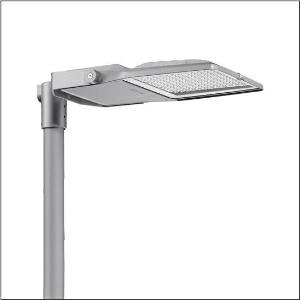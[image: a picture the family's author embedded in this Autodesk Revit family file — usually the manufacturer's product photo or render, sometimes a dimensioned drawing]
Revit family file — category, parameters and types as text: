
# Revit family: floodlight_fl_21_iq_midi___pl64_5xa7781f4e3a_1626
name_source: partatom
category: Lighting Fixtures
units: mm (PartAtom-declared; Revit-internal decimal feet)

## family parameters
Cut with Voids When Loaded = No
Host = Face
Light Source = No
Part Type = Normal
Room Calculation Point = No
Round Connector Dimension = Use Diameter
Shared = No

## types (1)
- --- (1 x LED, 36050 lm, 270.2 W, 4000K)
    Apparent Load = 270 VA
    CIE Flux Codes = 28 80 98 100 100
    Color Rendering = 70
    Color Temperature = 4000K
    Default Elevation = 1800 mm
    Description = Floodlight FL 21 iQ midi, floodlight, primary light control with lens, of PMMA, primary optical cover: protective disc, of toughened safety glass, transparent, light distribution: PL64, light emission: direct distribution, installation type: surface-mounted, lamps: LED, High Power LED, rated values: 36.050lm | 270,2W | 133,4lm/W (begin service life); end service life: 36.050lm | 286,6W; at 50% lumin. flux: 18.025lm | 117,7W | 153,1lm/W, colour temperature: 4000K, colour rendering: CRI > 70, light colour: 740, light setting 1 begin service life: 100% | 36.050lm | 270,2W | 133,4lm/W | 4.000K, light setting 1 end service life: 286,6W, further light settings possible, control: optimised constant luminous flux control (CLO 2.0), Desk-Remote (wireless, voltage-free reading and setting of iQ features in the workshop via application-optimized NFC function/RFID function), Light-Fading, Smart-Wire, Night-Set, Lumen-Switch, Temp-Guard, Auto-Match, with terminal, 6-pole, mains connection: 220..240V, AC, 50/60Hz, luminaire housing, of diecast aluminium, powder-coated, Siteco® metallic grey (DB 702S), corrosivity category C5 mid according to DIN EN ISO 12944suitable for swimming poolschlorine-resistant, sealing non-destructively replaceable, please order mast flange separately, mast bracket, of steel, galvanised, powder-coated, Siteco® metallic grey (DB 702S), protection rating (complete): IP66, insulation class (complete): insulation class II (safety insulation), certification: CE, ENEC, VDE, protection symbol: D, impact resistance: IK08, permissible operating ambient temperature: -40..+40°C, permissible operating ambient temperature for outdoor applications: -40..+50°C, standard: DIN EN 12944, LABS conformity tested according to VDMA 24364:2018-05, packaging unit: 1 piece

Light Distribution: PL64
    Height = 76 mm
    Lamp = 1 x LED
    Lamp Light Flux = 36050 lm
    Lamp Power = 270.2 W
    Lamp count = 1
    Length = 657 mm
    Luminous efficacy = 133 lm/W
    Manufacturer = Siteco
    ModVariant = No
    Model = 5XA7781F4E3A
    Number of Poles = 1
    OnlyDefault = Yes
    Power Factor = 1
    Product Name = Floodlight FL 21 iQ midi | PL64
    Product group = floodlight | pylon annexe
    ProductGroupID = 6201
    Protection Class = Protection class II
    Protection Degree = IP 66
    RLX_Detail_Level = 1
    RLX_Emergency_Light_Flux = 0 lm
    RLX_Emergency_Type = 0
    RLX_Emergency_Type_DB = No
    RlxData = <blob elided: 153945 chars, md5=ff08ab63>
    Socket = socket
    Standby Power = 0 W
    System Light Flux = 36050 lm
    System Power = 270 W
    Type Comments = factory setting: luminous flux: 100 % | dim-lin: 254 | 620 mA
    Type Image = l_1007123.jpg
    URL = http://relux.com
    VarID = @adj_110695
    Voltage = 0 V
    Weight = 0.00 kg
    Width = 442 mm

## geometry (parser evidence)
native form markers: Blend x4, Sweep x11
no freeform markers — native parametric forms only
